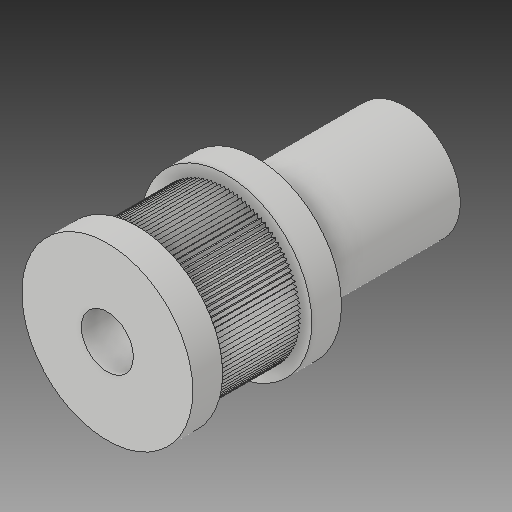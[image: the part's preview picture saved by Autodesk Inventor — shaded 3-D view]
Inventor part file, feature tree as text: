
AUTODESK INVENTOR PART (.ipt)
format: ipt  version: 2019 (Build 230136000, 136)  size: 570,368 bytes
history: native  units: mm
features: extrude x5, sketch x5, pattern_circular x1, plane x1, mirror x1
ambient origin geometry x8: Origin, YZ Plane, XZ Plane, XY Plane, X Axis, Y Axis, Z Axis, Center Point
bodies: Solid1 (feature_tree)
feature tree (13):
  extrude  "Extrusion1"  Depth=20.0mm TaperAngle=0.0deg
  extrude  "Extrusion2"  TaperAngle=30.0deg  [1 undecoded]
  pattern_circular  "Circular Pattern1"  Count=2  [1 undecoded]
  extrude  "Extrusion3"  Depth=20.0mm TaperAngle=360.0deg
  plane  "Work Plane1"
  mirror  "Mirror1"
  extrude  "Extrusion5"  Depth=20.0mm
  extrude  "Extrusion4"  Depth=4.0mm TaperAngle=0.0deg
  sketch  "Sketch1"  dims[d0=20.0mm d1=20.0mm d2=0.0mm]
  sketch  "Sketch2"  dims[d3=30.0deg d9=30.0deg]
  sketch  "Sketch3"  dims[d10=30.0deg]
  sketch  "Sketch4"  dims[d11=0.5mm]
  sketch  "Sketch5"  dims[d12=0.5mm d13=20.0mm d14=0.0mm d15=1080.0mm d16=360.0deg d18=23.0mm d19=4.0mm d20=0.0mm d21=10.0mm d22=7.0mm d23=40.0mm d24=0.0mm d25=15.0mm d26=20.0mm d27=0.0mm]
note: 2 required parameter values undecoded (feature->parameter linkage not recoverable at this tier; creation-order binding heuristic only, values carry confidence <= 0.55)
